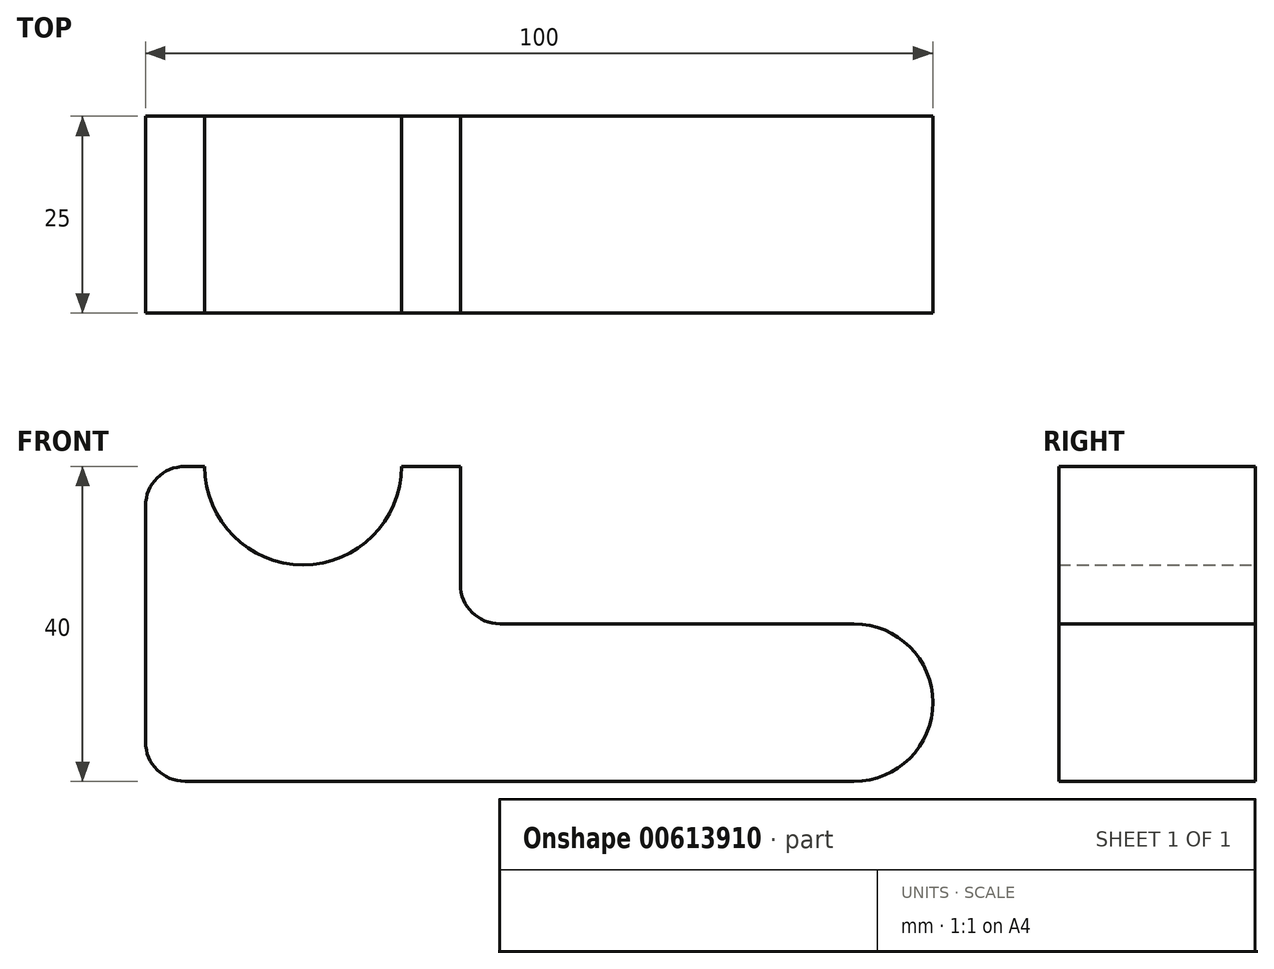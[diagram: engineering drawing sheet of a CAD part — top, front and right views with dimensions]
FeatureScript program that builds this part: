
annotation { "Feature Type Name" : "Feature", "Feature Type Description" : "" }
export const myFeature = defineFeature(function(context is Context, id is Id, definition is map)
    precondition{}
    {
        {
            var Q0;
            Q0=qCreatedBy(makeId("Front.planeOp"),FACE);
            var sketch = newSketch(context, id + "F0", { "sketchPlane" : qUnion([Q0])});
            skLineSegment(sketch, "E0", {"start": v(-49.4, 32.83) * mm, "end": v(-46.9, 32.83) * mm});
            skLineSegment(sketch, "E1", {"start": v(-14.4, 32.83) * mm, "end": v(-14.4, 17.83) * mm});
            skLineSegment(sketch, "E2", {"start": v(-9.4, 12.83) * mm, "end": v(35.6, 12.83) * mm});
            skLineSegment(sketch, "E3", {"start": v(35.6, -7.17) * mm, "end": v(-49.4, -7.17) * mm});
            skLineSegment(sketch, "E4", {"start": v(-54.4, -2.17) * mm, "end": v(-54.4, 27.83) * mm});
            skArc(sketch, "E5", {"start": v(35.6, -7.17) * mm, "mid": v(45.6, 2.83) * mm, "end": v(35.6, 12.83) * mm});
            skArc(sketch, "E6", {"start": v(-46.9, 32.83) * mm, "mid": v(-34.4, 20.33) * mm, "end": v(-21.9, 32.83) * mm});
            skLineSegment(sketch, "E7.trimOffspring", {"start": v(-21.9, 32.83) * mm, "end": v(-14.4, 32.83) * mm});
            skPoint(sketch, "E8.visualSharp", {"position": v(-54.4, 32.83) * mm});
            skArc(sketch, "E8.filletArc", {"start": v(-49.4, 32.83) * mm, "mid": v(-52.94, 31.37) * mm, "end": v(-54.4, 27.83) * mm});
            skPoint(sketch, "E9.visualSharp", {"position": v(-54.4, -7.17) * mm});
            skArc(sketch, "E9.filletArc", {"start": v(-54.4, -2.17) * mm, "mid": v(-52.94, -5.7) * mm, "end": v(-49.4, -7.17) * mm});
            skPoint(sketch, "E10.visualSharp", {"position": v(-14.4, 12.83) * mm});
            skArc(sketch, "E10.filletArc", {"start": v(-14.4, 17.83) * mm, "mid": v(-12.94, 14.3) * mm, "end": v(-9.4, 12.83) * mm});
            skSolve(sketch);
        }
        {
            var Q0;
            Q0 = qSketchRegion(id + "F0", true);
            extrude(context, id + "F1", {"entities" : qUnion([Q0]), "depth" : 25 * mm, "offsetDistance" : 25 * mm});
        }
    });
